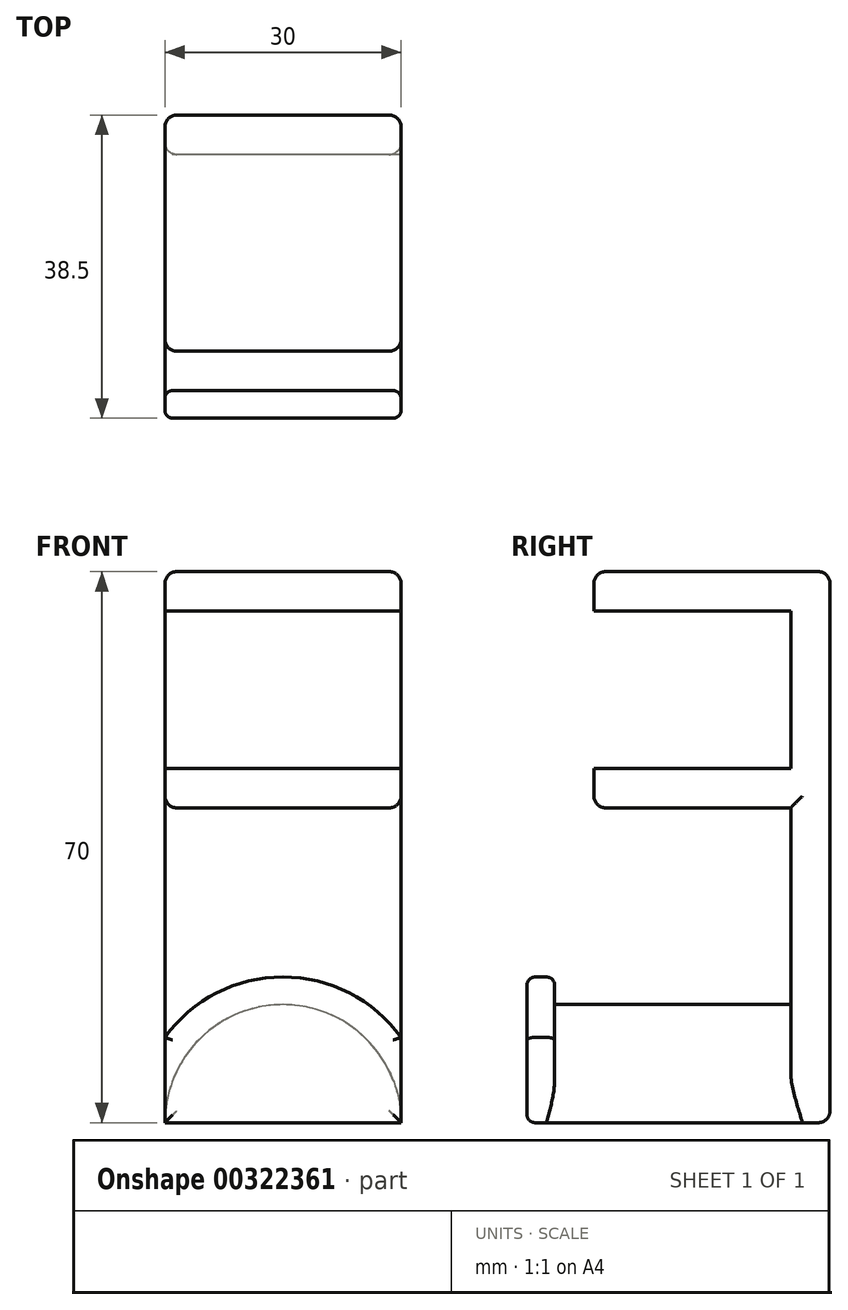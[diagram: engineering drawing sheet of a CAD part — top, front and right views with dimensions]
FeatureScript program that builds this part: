
annotation { "Feature Type Name" : "Feature", "Feature Type Description" : "" }
export const myFeature = defineFeature(function(context is Context, id is Id, definition is map)
    precondition{}
    {
        {
            var Q0;
            Q0=qCreatedBy(makeId("Front.planeOp"),FACE);
            var sketch = newSketch(context, id + "F0", { "sketchPlane" : qUnion([Q0])});
            skLineSegment(sketch, "E0.bottom", {"start": v(-15, 25) * mm, "end": v(15, 25) * mm});
            skLineSegment(sketch, "E0.top", {"start": v(-15, -45) * mm, "end": v(15, -45) * mm});
            skLineSegment(sketch, "E0.left", {"start": v(-15, 25) * mm, "end": v(-15, -45) * mm});
            skLineSegment(sketch, "E0.right", {"start": v(15, 25) * mm, "end": v(15, -45) * mm});
            skLineSegment(sketch, "E1", {"start": v(-15, 20) * mm, "end": v(15, 20) * mm});
            skLineSegment(sketch, "E2", {"start": v(-15, 0) * mm, "end": v(15, 0) * mm});
            skLineSegment(sketch, "E3", {"start": v(-15, -5) * mm, "end": v(15, -5) * mm});
            skPoint(sketch, "E4", {"position": v(0, 0) * mm});
            skArc(sketch, "E5", {"start": v(15, -45) * mm, "mid": v(0, -30) * mm, "end": v(-15, -45) * mm});
            skSolve(sketch);
        }
        {
            var Q0;
            Q0 = qSketchRegion(id + "F0", true);
            extrude(context, id + "F1", {"entities" : qUnion([Q0]), "depth" : 5 * mm});
        }
        {
            var Q0;
            {var subQ0=sQuery(id+"F0.wireOp",EDGE,"E0.bottom");Q0=makeQuery(id+"F0.imprint","IMPRINT",FACE,{"disambiguationData":[TD([[makeQuery(id+"F0.imprint","IMPRINT",EDGE,{"derivedFrom":subQ0}),-1.0]])]});}
            var Q1;
            {var subQ0=sQuery(id+"F0.wireOp",EDGE,"E2");Q1=makeQuery(id+"F0.imprint","IMPRINT",FACE,{"disambiguationData":[TD([[makeQuery(id+"F0.imprint","IMPRINT",EDGE,{"derivedFrom":subQ0}),-1.0]])]});}
            extrude(context, id + "F2", {"entities" : qUnion([Q0, Q1]), "operationType" : NewBodyOperationType.ADD, "depth" : 30 * mm});
        }
        {
            var Q0;
            Q0=makeQuery(id+"F0.imprint","IMPRINT",FACE,{"disambiguationData":[TD([[makeQuery(id+"F0.imprint","IMPRINT",EDGE,{"derivedFrom":sQuery(id+"F0.wireOp",EDGE,"E0.top")}),1.0]])]});
            extrude(context, id + "F3", {"entities" : qUnion([Q0]), "operationType" : NewBodyOperationType.ADD, "depth" : 35 * mm});
        }
        {
            var Q0;
            Q0=makeQuery(id+"F3.opExtrude","CAP_FACE",FACE,{"disambiguationData":[OSD([sQuery(id+"F0.wireOp",EDGE,"E0.top"),sQuery(id+"F0.wireOp",EDGE,"E5")])],"isStart":false});
            var sketch = newSketch(context, id + "F4", { "sketchPlane" : qUnion([Q0])});
            skArc(sketch, "E6", {"start": v(15, -34.17) * mm, "mid": v(0, -26.5) * mm, "end": v(-15, -34.17) * mm});
            skLineSegment(sketch, "E7", {"start": v(-15, -45) * mm, "end": v(15, -45) * mm, "construction": true});
            skLineSegment(sketch, "E8.0", {"start": v(-15, -34.17) * mm, "end": v(-15, -45) * mm});
            skLineSegment(sketch, "E8.1", {"start": v(15, -34.17) * mm, "end": v(15, -45) * mm});
            skPoint(sketch, "E9.orphan", {"position": v(-15, 25) * mm});
            skPoint(sketch, "E10.orphan", {"position": v(15, 25) * mm});
            skSolve(sketch);
        }
        {
            var Q0;
            Q0=makeQuery(id+"F4.imprint","IMPRINT",FACE,{"disambiguationData":[TD([[makeQuery(id+"F4.imprint","IMPRINT",EDGE,{"derivedFrom":sQuery(id+"F4.wireOp",EDGE,"E6")}),1.0]])]});
            var Q1;
            Q1=makeQuery(id+"F4.imprint","IMPRINT",FACE,{"disambiguationData":[TD([[makeQuery(id+"F4.imprint","IMPRINT",EDGE,{"derivedFrom":makeQuery(id+"F3.opExtrude","CAP_EDGE",EDGE,{"disambiguationData":[OSD([sQuery(id+"F0.wireOp",EDGE,"E0.top")])],"isStart":false})}),1.0]])]});
            extrude(context, id + "F5", {"entities" : qUnion([Q0, Q1]), "operationType" : NewBodyOperationType.ADD, "depth" : 3.5 * mm});
        }
        {
            var Q0;
            {var subQ0=sQuery(id+"F0.wireOp",EDGE,"E0.right");var subQ1=sQuery(id+"F0.wireOp",EDGE,"E0.bottom");Q0=makeQuery(id+"F2.boolean.opBoolean","MERGE",EDGE,{"derivedFrom":[makeQuery(id+"F1.opExtrude","SWEPT_EDGE",EDGE,{"disambiguationData":[OSD([subQ1,subQ0])]}),makeQuery(id+"F2.opExtrude","SWEPT_EDGE",EDGE,{"disambiguationData":[OSD([subQ1,subQ0])]})]});}
            var Q1;
            Q1=makeQuery(id+"F2.opExtrude","CAP_EDGE",EDGE,{"disambiguationData":[OSD([sQuery(id+"F0.wireOp",EDGE,"E0.bottom")])],"isStart":false});
            var Q2;
            {var subQ0=sQuery(id+"F0.wireOp",EDGE,"E0.right");Q2=makeQuery(id+"F2.opExtrude","CAP_EDGE",EDGE,{"disambiguationData":[OSD([subQ0]),TDD([makeQuery(id+"F0.imprint","IMPRINT",EDGE,{"disambiguationData":[TD([[makeQuery(id+"F0.imprint","INTERSECT",VERTEX,{"derivedFrom":[sQuery(id+"F0.wireOp",EDGE,"E0.bottom"),subQ0]}),-1.0]])],"derivedFrom":subQ0})])],"isStart":false});}
            var Q3;
            {var subQ0=sQuery(id+"F0.wireOp",EDGE,"E0.left");Q3=makeQuery(id+"F2.opExtrude","CAP_EDGE",EDGE,{"disambiguationData":[OSD([subQ0]),TDD([makeQuery(id+"F0.imprint","IMPRINT",EDGE,{"disambiguationData":[TD([[makeQuery(id+"F0.imprint","INTERSECT",VERTEX,{"derivedFrom":[sQuery(id+"F0.wireOp",EDGE,"E0.bottom"),subQ0]}),-1.0]])],"derivedFrom":subQ0})])],"isStart":false});}
            var Q4;
            {var subQ0=sQuery(id+"F0.wireOp",EDGE,"E0.left");var subQ1=sQuery(id+"F0.wireOp",EDGE,"E0.bottom");Q4=makeQuery(id+"F2.boolean.opBoolean","MERGE",EDGE,{"derivedFrom":[makeQuery(id+"F1.opExtrude","SWEPT_EDGE",EDGE,{"disambiguationData":[OSD([subQ1,subQ0])]}),makeQuery(id+"F2.opExtrude","SWEPT_EDGE",EDGE,{"disambiguationData":[OSD([subQ1,subQ0])]})]});}
            var Q5;
            Q5=makeQuery(id+"F2.opExtrude","SWEPT_EDGE",EDGE,{"disambiguationData":[OSD([sQuery(id+"F0.wireOp",EDGE,"E0.left"),sQuery(id+"F0.wireOp",EDGE,"E3")])]});
            var Q6;
            {var subQ0=sQuery(id+"F0.wireOp",EDGE,"E0.left");var subQ3=sQuery(id+"F0.wireOp",EDGE,"E0.top");Q6=makeQuery(id+"F2.boolean.opBoolean","SPLIT",EDGE,{"disambiguationData":[TD([makeQuery(id+"F1.opExtrude","SWEPT_FACE",FACE,{"disambiguationData":[OSD([subQ3])]})])],"derivedFrom":makeQuery(id+"F1.opExtrude","CAP_EDGE",EDGE,{"disambiguationData":[OSD([subQ0])],"isStart":false})});}
            var Q7;
            {var subQ0=sQuery(id+"F0.wireOp",EDGE,"E0.left");Q7=makeQuery(id+"F2.opExtrude","CAP_EDGE",EDGE,{"disambiguationData":[OSD([subQ0]),TDD([makeQuery(id+"F0.imprint","IMPRINT",EDGE,{"disambiguationData":[TD([[makeQuery(id+"F0.imprint","INTERSECT",VERTEX,{"derivedFrom":[subQ0,sQuery(id+"F0.wireOp",EDGE,"E2")]}),-1.0]])],"derivedFrom":subQ0})])],"isStart":false});}
            var Q8;
            Q8=makeQuery(id+"F2.opExtrude","CAP_EDGE",EDGE,{"disambiguationData":[OSD([sQuery(id+"F0.wireOp",EDGE,"E3")])],"isStart":false});
            var Q9;
            Q9=makeQuery(id+"F2.opExtrude","SWEPT_EDGE",EDGE,{"disambiguationData":[OSD([sQuery(id+"F0.wireOp",EDGE,"E0.right"),sQuery(id+"F0.wireOp",EDGE,"E3")])]});
            var Q10;
            {var subQ0=sQuery(id+"F0.wireOp",EDGE,"E0.right");Q10=makeQuery(id+"F2.opExtrude","CAP_EDGE",EDGE,{"disambiguationData":[OSD([subQ0]),TDD([makeQuery(id+"F0.imprint","IMPRINT",EDGE,{"disambiguationData":[TD([[makeQuery(id+"F0.imprint","INTERSECT",VERTEX,{"derivedFrom":[subQ0,sQuery(id+"F0.wireOp",EDGE,"E2")]}),-1.0]])],"derivedFrom":subQ0})])],"isStart":false});}
            var Q11;
            {var subQ0=sQuery(id+"F0.wireOp",EDGE,"E0.right");var subQ2=sQuery(id+"F0.wireOp",EDGE,"E0.top");Q11=makeQuery(id+"F2.boolean.opBoolean","SPLIT",EDGE,{"disambiguationData":[TD([makeQuery(id+"F1.opExtrude","SWEPT_FACE",FACE,{"disambiguationData":[OSD([subQ2])]})])],"derivedFrom":makeQuery(id+"F1.opExtrude","CAP_EDGE",EDGE,{"disambiguationData":[OSD([subQ0])],"isStart":false})});}
            var Q12;
            Q12=makeQuery(id+"F1.opExtrude","CAP_EDGE",EDGE,{"disambiguationData":[OSD([sQuery(id+"F0.wireOp",EDGE,"E0.left")])],"isStart":true});
            var Q13;
            Q13=makeQuery(id+"F1.opExtrude","CAP_EDGE",EDGE,{"disambiguationData":[OSD([sQuery(id+"F0.wireOp",EDGE,"E0.right")])],"isStart":true});
            var Q14;
            Q14=makeQuery(id+"F1.opExtrude","CAP_EDGE",EDGE,{"disambiguationData":[OSD([sQuery(id+"F0.wireOp",EDGE,"E0.bottom")])],"isStart":true});
            var Q15;
            Q15=makeQuery(id+"F1.opExtrude","CAP_EDGE",EDGE,{"disambiguationData":[OSD([sQuery(id+"F0.wireOp",EDGE,"E0.top")])],"isStart":true});
            fillet(context, id + "F6", {"entities" : qUnion([Q0, Q1, Q2, Q3, Q4, Q5, Q6, Q7, Q8, Q9, Q10, Q11, Q12, Q13, Q14, Q15]), "radius" : 1.5 * mm, "tangentPropagation" : true, "allowEdgeOverflow" : false});
        }
        {
            var Q0;
            Q0=makeQuery(id+"F5.opExtrude","CAP_EDGE",EDGE,{"disambiguationData":[OSD([sQuery(id+"F4.wireOp",EDGE,"E8.1")])],"isStart":false});
            var Q1;
            Q1=makeQuery(id+"F5.opExtrude","CAP_EDGE",EDGE,{"disambiguationData":[OSD([sQuery(id+"F4.wireOp",EDGE,"E6")])],"isStart":false});
            var Q2;
            Q2=makeQuery(id+"F5.opExtrude","CAP_EDGE",EDGE,{"disambiguationData":[OSD([sQuery(id+"F4.wireOp",EDGE,"E8.0")])],"isStart":false});
            var Q3;
            Q3=makeQuery(id+"F5.opExtrude","CAP_EDGE",EDGE,{"disambiguationData":[OSD([sQuery(id+"F4.wireOp",EDGE,"E6")])],"isStart":true});
            var Q4;
            Q4=makeQuery(id+"F5.opExtrude","CAP_EDGE",EDGE,{"disambiguationData":[OSD([sQuery(id+"F4.wireOp",EDGE,"E8.1")])],"isStart":true});
            var Q5;
            Q5=makeQuery(id+"F5.opExtrude","CAP_EDGE",EDGE,{"disambiguationData":[OSD([sQuery(id+"F4.wireOp",EDGE,"E8.0")])],"isStart":true});
            var Q6;
            Q6=makeQuery(id+"F5.opExtrude","CAP_EDGE",EDGE,{"disambiguationData":[OSD([sQuery(id+"F0.wireOp",EDGE,"E0.top")])],"isStart":false});
            fillet(context, id + "F7", {"entities" : qUnion([Q0, Q1, Q2, Q3, Q4, Q5, Q6]), "radius" : 1 * mm, "tangentPropagation" : true, "allowEdgeOverflow" : false});
        }
    });
